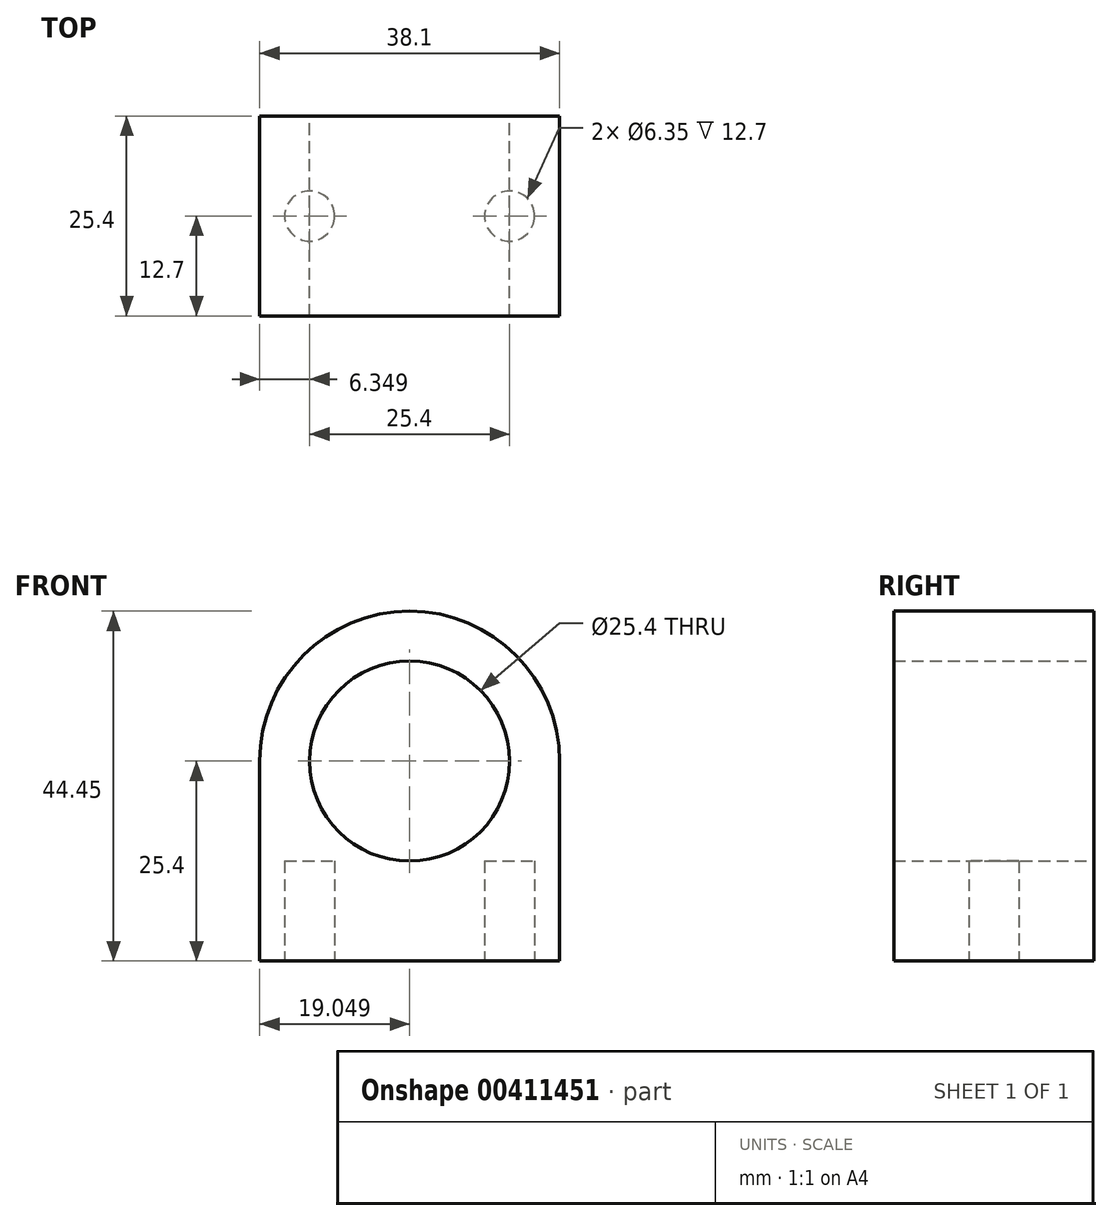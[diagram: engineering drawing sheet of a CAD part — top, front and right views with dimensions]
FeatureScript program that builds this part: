
annotation { "Feature Type Name" : "Feature", "Feature Type Description" : "" }
export const myFeature = defineFeature(function(context is Context, id is Id, definition is map)
    precondition{}
    {
        {
            var Q0;
            Q0=qCreatedBy(makeId("Front.planeOp"),FACE);
            var sketch = newSketch(context, id + "F0", { "sketchPlane" : qUnion([Q0])});
            skLineSegment(sketch, "E0.bottom", {"start": v(-14.6, 0) * mm, "end": v(23.5, 0) * mm});
            skLineSegment(sketch, "E0.left", {"start": v(-14.6, 0) * mm, "end": v(-14.6, 25.4) * mm});
            skLineSegment(sketch, "E0.right", {"start": v(23.5, 0) * mm, "end": v(23.5, 25.4) * mm});
            skArc(sketch, "E1", {"start": v(23.5, 25.4) * mm, "mid": v(4.45, 44.45) * mm, "end": v(-14.6, 25.4) * mm});
            skCircle(sketch, "E2", {"center": v(4.45, 25.4) * mm, "radius": 12.7 * mm});
            skSolve(sketch);
        }
        {
            var Q0;
            Q0=makeQuery(id+"F0.imprint","IMPRINT",FACE,{"disambiguationData":[TD([[makeQuery(id+"F0.imprint","IMPRINT",EDGE,{"derivedFrom":sQuery(id+"F0.wireOp",EDGE,"E0.bottom")}),1.0]])]});
            extrude(context, id + "F1", {"entities" : qUnion([Q0]), "depth" : 25.4 * mm});
        }
        {
            var Q0;
            Q0=makeQuery(id+"F1.opExtrude","SWEPT_FACE",FACE,{"disambiguationData":[OSD([sQuery(id+"F0.wireOp",EDGE,"E0.bottom")])]});
            var sketch = newSketch(context, id + "F2", { "sketchPlane" : qUnion([Q0])});
            skCircle(sketch, "E3", {"center": v(17.15, 12.7) * mm, "radius": 3.18 * mm});
            skCircle(sketch, "E4", {"center": v(-8.25, 12.7) * mm, "radius": 3.18 * mm});
            skSolve(sketch);
        }
        {
            var Q0;
            Q0=makeQuery(id+"F2.imprint","IMPRINT",FACE,{"disambiguationData":[TD([[makeQuery(id+"F2.imprint","IMPRINT",EDGE,{"derivedFrom":sQuery(id+"F2.wireOp",EDGE,"E4")}),1.0]])]});
            var Q1;
            Q1=makeQuery(id+"F2.imprint","IMPRINT",FACE,{"disambiguationData":[TD([[makeQuery(id+"F2.imprint","IMPRINT",EDGE,{"derivedFrom":sQuery(id+"F2.wireOp",EDGE,"E3")}),1.0]])]});
            extrude(context, id + "F3", {"entities" : qUnion([Q0, Q1]), "operationType" : NewBodyOperationType.REMOVE, "oppositeDirection" : true, "depth" : 12.7 * mm});
        }
    });
